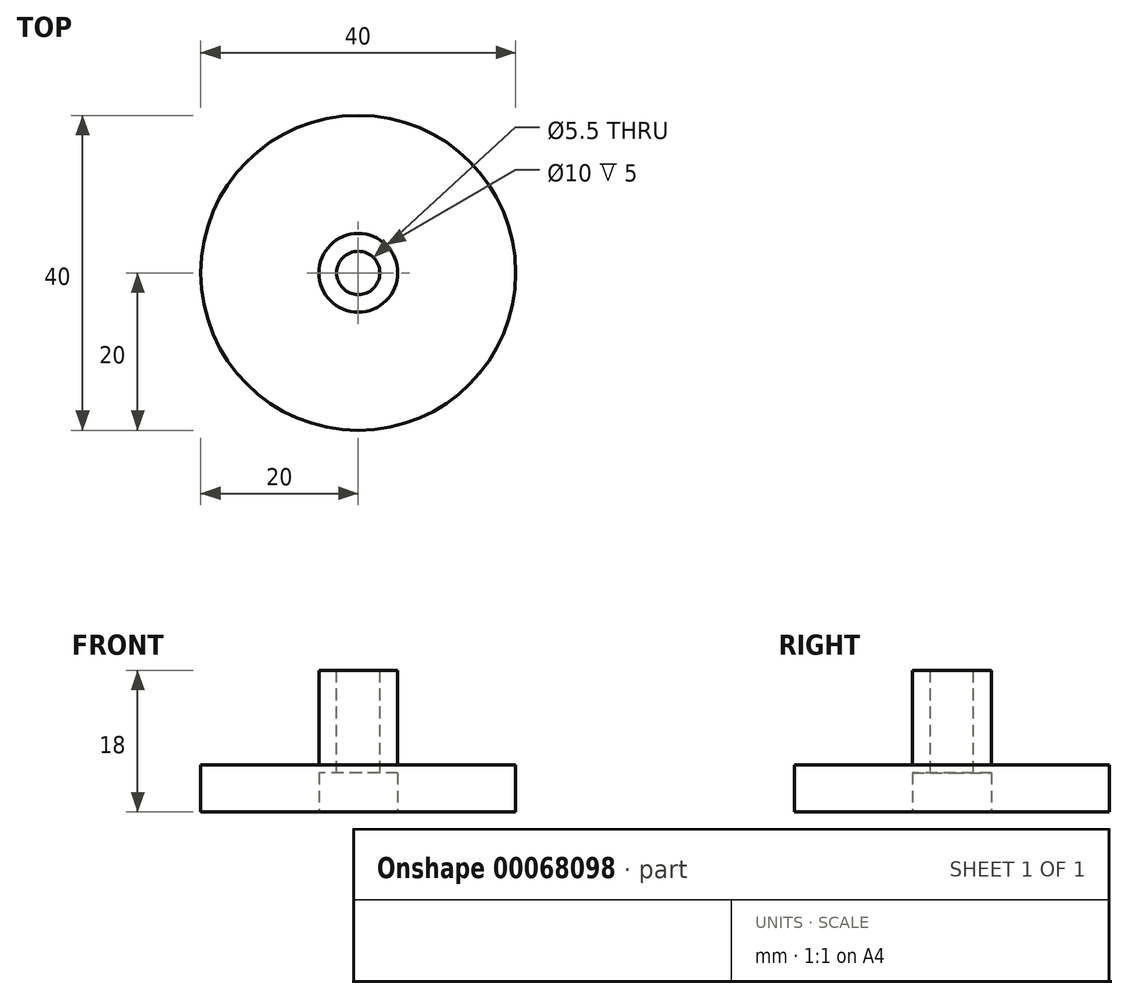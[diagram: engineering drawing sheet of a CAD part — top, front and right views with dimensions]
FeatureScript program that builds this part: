
annotation { "Feature Type Name" : "Feature", "Feature Type Description" : "" }
export const myFeature = defineFeature(function(context is Context, id is Id, definition is map)
    precondition{}
    {
        {
            var Q0;
            Q0=qCreatedBy(makeId("Top.planeOp"),FACE);
            var sketch = newSketch(context, id + "F0", { "sketchPlane" : qUnion([Q0])});
            skCircle(sketch, "E0", {"center": v(0, 0) * mm, "radius": 20 * mm});
            skSolve(sketch);
        }
        {
            var Q0;
            Q0=makeQuery(id+"F0.imprint","IMPRINT",FACE,{"disambiguationData":[TD([[makeQuery(id+"F0.imprint","IMPRINT",EDGE,{"derivedFrom":sQuery(id+"F0.wireOp",EDGE,"E0")}),1.0]])]});
            extrude(context, id + "F1", {"entities" : qUnion([Q0]), "depth" : 6 * mm});
        }
        {
            var Q0;
            Q0=makeQuery(id+"F1.opExtrude","CAP_FACE",FACE,{"disambiguationData":[OSD([sQuery(id+"F0.wireOp",EDGE,"E0")])],"isStart":false});
            var sketch = newSketch(context, id + "F2", { "sketchPlane" : qUnion([Q0])});
            skCircle(sketch, "E1", {"center": v(0, 0) * mm, "radius": 5 * mm});
            skSolve(sketch);
        }
        {
            var Q0;
            Q0 = qSketchRegion(id + "F2", true);
            extrude(context, id + "F3", {"entities" : qUnion([Q0]), "operationType" : NewBodyOperationType.ADD, "depth" : 12 * mm});
        }
        {
            var Q0;
            Q0=makeQuery(id+"F3.opExtrude","CAP_FACE",FACE,{"disambiguationData":[OSD([sQuery(id+"F2.wireOp",EDGE,"E1")])],"isStart":false});
            var sketch = newSketch(context, id + "F4", { "sketchPlane" : qUnion([Q0])});
            skCircle(sketch, "E2", {"center": v(0, 0) * mm, "radius": 2.75 * mm});
            skSolve(sketch);
        }
        {
            var Q0;
            Q0=makeQuery(id+"F4.imprint","IMPRINT",FACE,{"disambiguationData":[TD([[makeQuery(id+"F4.imprint","IMPRINT",EDGE,{"derivedFrom":sQuery(id+"F4.wireOp",EDGE,"E2")}),1.0]])]});
            extrude(context, id + "F5", {"entities" : qUnion([Q0]), "operationType" : NewBodyOperationType.REMOVE, "endBound" : BoundingType.THROUGH_ALL, "oppositeDirection" : true, "depth" : 18 * mm});
        }
        {
            var Q0;
            Q0=makeQuery(id+"F0.imprint","IMPRINT",FACE,{"disambiguationData":[TD([[makeQuery(id+"F0.imprint","IMPRINT",EDGE,{"derivedFrom":sQuery(id+"F0.wireOp",EDGE,"E0")}),1.0]])]});
            var sketch = newSketch(context, id + "F6", { "sketchPlane" : qUnion([Q0])});
            skCircle(sketch, "E3", {"center": v(0, 0) * mm, "radius": 5 * mm});
            skSolve(sketch);
        }
        {
            var Q0;
            Q0=makeQuery(id+"F6.imprint","IMPRINT",FACE,{"disambiguationData":[TD([[makeQuery(id+"F6.imprint","IMPRINT",EDGE,{"derivedFrom":sQuery(id+"F6.wireOp",EDGE,"E3")}),1.0]])]});
            extrude(context, id + "F7", {"entities" : qUnion([Q0]), "operationType" : NewBodyOperationType.REMOVE, "depth" : 5 * mm});
        }
    });
